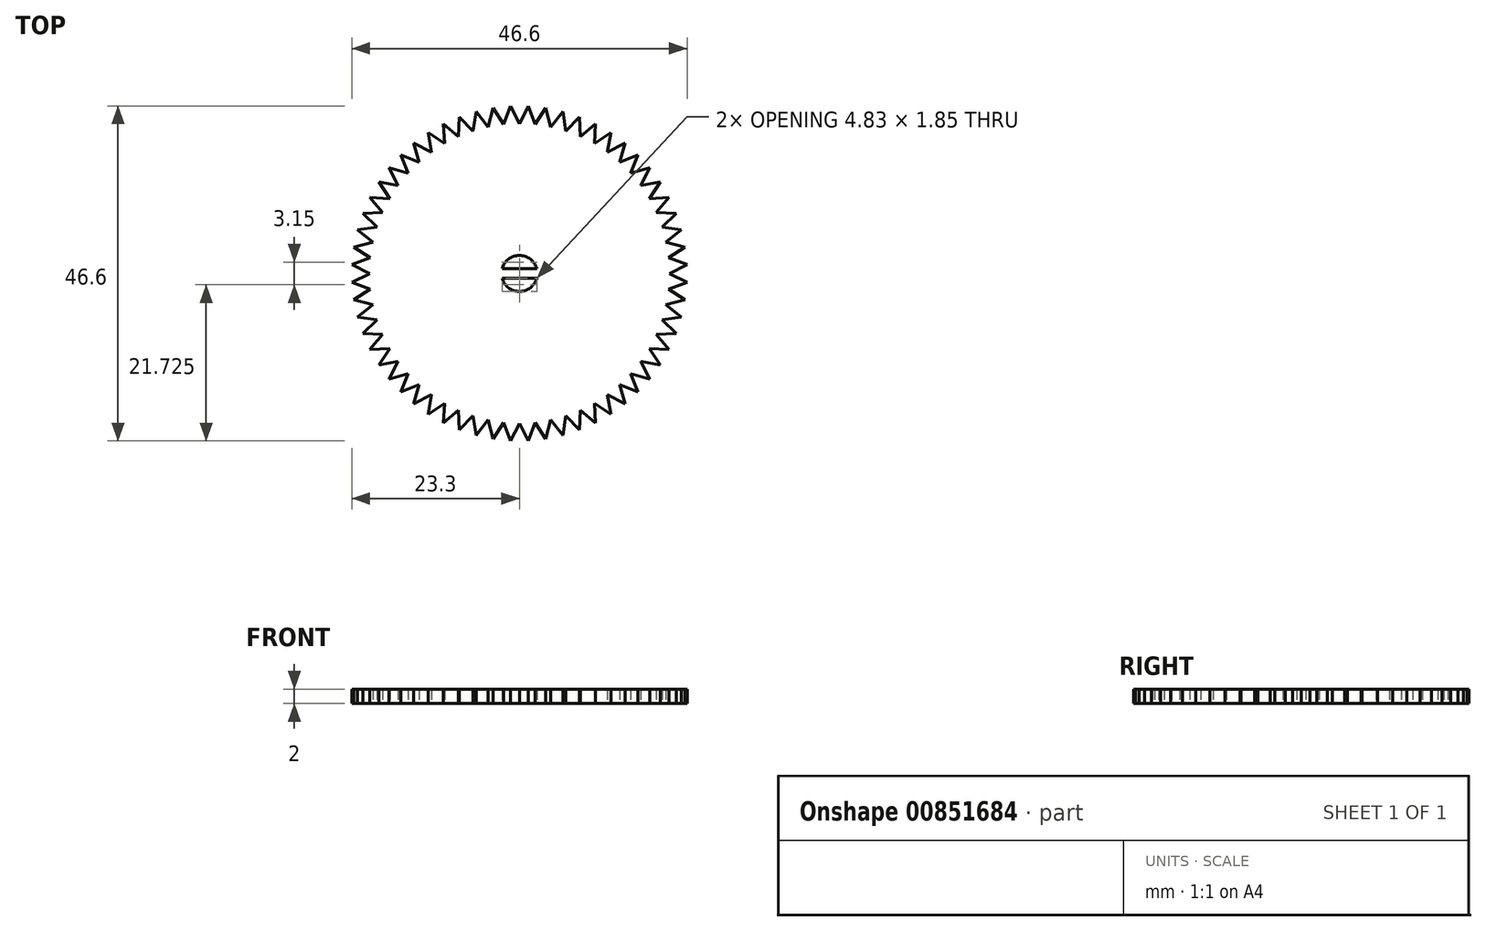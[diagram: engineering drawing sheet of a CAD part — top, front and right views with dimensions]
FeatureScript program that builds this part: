
annotation { "Feature Type Name" : "Feature", "Feature Type Description" : "" }
export const myFeature = defineFeature(function(context is Context, id is Id, definition is map)
    precondition{}
    {
        {
            var Q0;
            Q0=qCreatedBy(makeId("Top.planeOp"),FACE);
            var sketch = newSketch(context, id + "F0", { "sketchPlane" : qUnion([Q0])});
            skLineSegment(sketch, "E0", {"start": v(0, 0) * mm, "end": v(0, 24.66) * mm, "construction": true});
            skLineSegment(sketch, "E1", {"start": v(0, 0) * mm, "end": v(1.3, 24.64) * mm, "construction": true});
            skLineSegment(sketch, "E2", {"start": v(0, 0) * mm, "end": v(2.57, 24.5) * mm, "construction": true});
            skLineSegment(sketch, "E3", {"start": v(0, 20.83) * mm, "end": v(1.22, 23.3) * mm});
            skLineSegment(sketch, "E4", {"start": v(1.22, 23.3) * mm, "end": v(2.18, 20.71) * mm});
            skLineSegment(sketch, "E5.1.0", {"start": v(-2.18, 20.71) * mm, "end": v(-1.22, 23.3) * mm});
            skLineSegment(sketch, "E5.1.1", {"start": v(-1.22, 23.3) * mm, "end": v(0, 20.83) * mm});
            skLineSegment(sketch, "E5.2.0", {"start": v(-4.33, 20.37) * mm, "end": v(-3.65, 23.04) * mm});
            skLineSegment(sketch, "E5.2.1", {"start": v(-3.65, 23.04) * mm, "end": v(-2.18, 20.71) * mm});
            skLineSegment(sketch, "E5.3.0", {"start": v(-6.44, 19.8) * mm, "end": v(-6.04, 22.53) * mm});
            skLineSegment(sketch, "E5.3.1", {"start": v(-6.04, 22.53) * mm, "end": v(-4.33, 20.37) * mm});
            skLineSegment(sketch, "E5.4.0", {"start": v(-8.47, 19.03) * mm, "end": v(-8.36, 21.78) * mm});
            skLineSegment(sketch, "E5.4.1", {"start": v(-8.36, 21.78) * mm, "end": v(-6.44, 19.8) * mm});
            skLineSegment(sketch, "E5.5.0", {"start": v(-10.41, 18.04) * mm, "end": v(-10.6, 20.78) * mm});
            skLineSegment(sketch, "E5.5.1", {"start": v(-10.6, 20.78) * mm, "end": v(-8.47, 19.03) * mm});
            skLineSegment(sketch, "E5.6.0", {"start": v(-12.24, 16.85) * mm, "end": v(-12.7, 19.56) * mm});
            skLineSegment(sketch, "E5.6.1", {"start": v(-12.7, 19.56) * mm, "end": v(-10.41, 18.04) * mm});
            skLineSegment(sketch, "E5.7.0", {"start": v(-13.94, 15.48) * mm, "end": v(-14.68, 18.13) * mm});
            skLineSegment(sketch, "E5.7.1", {"start": v(-14.68, 18.13) * mm, "end": v(-12.24, 16.85) * mm});
            skLineSegment(sketch, "E5.8.0", {"start": v(-15.48, 13.94) * mm, "end": v(-16.5, 16.5) * mm});
            skLineSegment(sketch, "E5.8.1", {"start": v(-16.5, 16.5) * mm, "end": v(-13.94, 15.48) * mm});
            skLineSegment(sketch, "E5.9.0", {"start": v(-16.85, 12.24) * mm, "end": v(-18.13, 14.68) * mm});
            skLineSegment(sketch, "E5.9.1", {"start": v(-18.13, 14.68) * mm, "end": v(-15.48, 13.94) * mm});
            skLineSegment(sketch, "E5.10.0", {"start": v(-18.04, 10.41) * mm, "end": v(-19.56, 12.7) * mm});
            skLineSegment(sketch, "E5.10.1", {"start": v(-19.56, 12.7) * mm, "end": v(-16.85, 12.24) * mm});
            skLineSegment(sketch, "E5.11.0", {"start": v(-19.03, 8.47) * mm, "end": v(-20.78, 10.6) * mm});
            skLineSegment(sketch, "E5.11.1", {"start": v(-20.78, 10.6) * mm, "end": v(-18.04, 10.41) * mm});
            skLineSegment(sketch, "E5.12.0", {"start": v(-19.8, 6.44) * mm, "end": v(-21.78, 8.36) * mm});
            skLineSegment(sketch, "E5.12.1", {"start": v(-21.78, 8.36) * mm, "end": v(-19.03, 8.47) * mm});
            skLineSegment(sketch, "E5.13.0", {"start": v(-20.37, 4.33) * mm, "end": v(-22.53, 6.04) * mm});
            skLineSegment(sketch, "E5.13.1", {"start": v(-22.53, 6.04) * mm, "end": v(-19.8, 6.44) * mm});
            skLineSegment(sketch, "E5.14.0", {"start": v(-20.71, 2.18) * mm, "end": v(-23.04, 3.65) * mm});
            skLineSegment(sketch, "E5.14.1", {"start": v(-23.04, 3.65) * mm, "end": v(-20.37, 4.33) * mm});
            skLineSegment(sketch, "E5.15.0", {"start": v(-20.83, 0) * mm, "end": v(-23.3, 1.22) * mm});
            skLineSegment(sketch, "E5.15.1", {"start": v(-23.3, 1.22) * mm, "end": v(-20.71, 2.18) * mm});
            skLineSegment(sketch, "E5.16.0", {"start": v(-20.71, -2.18) * mm, "end": v(-23.3, -1.22) * mm});
            skLineSegment(sketch, "E5.16.1", {"start": v(-23.3, -1.22) * mm, "end": v(-20.83, 0) * mm});
            skLineSegment(sketch, "E5.17.0", {"start": v(-20.37, -4.33) * mm, "end": v(-23.04, -3.65) * mm});
            skLineSegment(sketch, "E5.17.1", {"start": v(-23.04, -3.65) * mm, "end": v(-20.71, -2.18) * mm});
            skLineSegment(sketch, "E5.18.0", {"start": v(-19.8, -6.44) * mm, "end": v(-22.53, -6.04) * mm});
            skLineSegment(sketch, "E5.18.1", {"start": v(-22.53, -6.04) * mm, "end": v(-20.37, -4.33) * mm});
            skLineSegment(sketch, "E5.19.0", {"start": v(-19.03, -8.47) * mm, "end": v(-21.78, -8.36) * mm});
            skLineSegment(sketch, "E5.19.1", {"start": v(-21.78, -8.36) * mm, "end": v(-19.8, -6.44) * mm});
            skLineSegment(sketch, "E5.20.0", {"start": v(-18.04, -10.41) * mm, "end": v(-20.78, -10.6) * mm});
            skLineSegment(sketch, "E5.20.1", {"start": v(-20.78, -10.6) * mm, "end": v(-19.03, -8.47) * mm});
            skLineSegment(sketch, "E5.21.0", {"start": v(-16.85, -12.24) * mm, "end": v(-19.56, -12.7) * mm});
            skLineSegment(sketch, "E5.21.1", {"start": v(-19.56, -12.7) * mm, "end": v(-18.04, -10.41) * mm});
            skLineSegment(sketch, "E5.22.0", {"start": v(-15.48, -13.94) * mm, "end": v(-18.13, -14.68) * mm});
            skLineSegment(sketch, "E5.22.1", {"start": v(-18.13, -14.68) * mm, "end": v(-16.85, -12.24) * mm});
            skLineSegment(sketch, "E5.23.0", {"start": v(-13.94, -15.48) * mm, "end": v(-16.5, -16.5) * mm});
            skLineSegment(sketch, "E5.23.1", {"start": v(-16.5, -16.5) * mm, "end": v(-15.48, -13.94) * mm});
            skLineSegment(sketch, "E5.24.0", {"start": v(-12.24, -16.85) * mm, "end": v(-14.68, -18.13) * mm});
            skLineSegment(sketch, "E5.24.1", {"start": v(-14.68, -18.13) * mm, "end": v(-13.94, -15.48) * mm});
            skLineSegment(sketch, "E5.25.0", {"start": v(-10.41, -18.04) * mm, "end": v(-12.7, -19.56) * mm});
            skLineSegment(sketch, "E5.25.1", {"start": v(-12.7, -19.56) * mm, "end": v(-12.24, -16.85) * mm});
            skLineSegment(sketch, "E5.26.0", {"start": v(-8.47, -19.03) * mm, "end": v(-10.6, -20.78) * mm});
            skLineSegment(sketch, "E5.26.1", {"start": v(-10.6, -20.78) * mm, "end": v(-10.41, -18.04) * mm});
            skLineSegment(sketch, "E5.27.0", {"start": v(-6.44, -19.8) * mm, "end": v(-8.36, -21.78) * mm});
            skLineSegment(sketch, "E5.27.1", {"start": v(-8.36, -21.78) * mm, "end": v(-8.47, -19.03) * mm});
            skLineSegment(sketch, "E5.28.0", {"start": v(-4.33, -20.37) * mm, "end": v(-6.04, -22.53) * mm});
            skLineSegment(sketch, "E5.28.1", {"start": v(-6.04, -22.53) * mm, "end": v(-6.44, -19.8) * mm});
            skLineSegment(sketch, "E5.29.0", {"start": v(-2.18, -20.71) * mm, "end": v(-3.65, -23.04) * mm});
            skLineSegment(sketch, "E5.29.1", {"start": v(-3.65, -23.04) * mm, "end": v(-4.33, -20.37) * mm});
            skLineSegment(sketch, "E5.30.0", {"start": v(0, -20.83) * mm, "end": v(-1.22, -23.3) * mm});
            skLineSegment(sketch, "E5.30.1", {"start": v(-1.22, -23.3) * mm, "end": v(-2.18, -20.71) * mm});
            skLineSegment(sketch, "E5.31.0", {"start": v(2.18, -20.71) * mm, "end": v(1.22, -23.3) * mm});
            skLineSegment(sketch, "E5.31.1", {"start": v(1.22, -23.3) * mm, "end": v(0, -20.83) * mm});
            skLineSegment(sketch, "E5.32.0", {"start": v(4.33, -20.37) * mm, "end": v(3.65, -23.04) * mm});
            skLineSegment(sketch, "E5.32.1", {"start": v(3.65, -23.04) * mm, "end": v(2.18, -20.71) * mm});
            skLineSegment(sketch, "E5.33.0", {"start": v(6.44, -19.8) * mm, "end": v(6.04, -22.53) * mm});
            skLineSegment(sketch, "E5.33.1", {"start": v(6.04, -22.53) * mm, "end": v(4.33, -20.37) * mm});
            skLineSegment(sketch, "E5.34.0", {"start": v(8.47, -19.03) * mm, "end": v(8.36, -21.78) * mm});
            skLineSegment(sketch, "E5.34.1", {"start": v(8.36, -21.78) * mm, "end": v(6.44, -19.8) * mm});
            skLineSegment(sketch, "E5.35.0", {"start": v(10.41, -18.04) * mm, "end": v(10.6, -20.78) * mm});
            skLineSegment(sketch, "E5.35.1", {"start": v(10.6, -20.78) * mm, "end": v(8.47, -19.03) * mm});
            skLineSegment(sketch, "E5.36.0", {"start": v(12.24, -16.85) * mm, "end": v(12.7, -19.56) * mm});
            skLineSegment(sketch, "E5.36.1", {"start": v(12.7, -19.56) * mm, "end": v(10.41, -18.04) * mm});
            skLineSegment(sketch, "E5.37.0", {"start": v(13.94, -15.48) * mm, "end": v(14.68, -18.13) * mm});
            skLineSegment(sketch, "E5.37.1", {"start": v(14.68, -18.13) * mm, "end": v(12.24, -16.85) * mm});
            skLineSegment(sketch, "E5.38.0", {"start": v(15.48, -13.94) * mm, "end": v(16.5, -16.5) * mm});
            skLineSegment(sketch, "E5.38.1", {"start": v(16.5, -16.5) * mm, "end": v(13.94, -15.48) * mm});
            skLineSegment(sketch, "E5.39.0", {"start": v(16.85, -12.24) * mm, "end": v(18.13, -14.68) * mm});
            skLineSegment(sketch, "E5.39.1", {"start": v(18.13, -14.68) * mm, "end": v(15.48, -13.94) * mm});
            skLineSegment(sketch, "E5.40.0", {"start": v(18.04, -10.41) * mm, "end": v(19.56, -12.7) * mm});
            skLineSegment(sketch, "E5.40.1", {"start": v(19.56, -12.7) * mm, "end": v(16.85, -12.24) * mm});
            skLineSegment(sketch, "E5.41.0", {"start": v(19.03, -8.47) * mm, "end": v(20.78, -10.6) * mm});
            skLineSegment(sketch, "E5.41.1", {"start": v(20.78, -10.6) * mm, "end": v(18.04, -10.41) * mm});
            skLineSegment(sketch, "E5.42.0", {"start": v(19.8, -6.44) * mm, "end": v(21.78, -8.36) * mm});
            skLineSegment(sketch, "E5.42.1", {"start": v(21.78, -8.36) * mm, "end": v(19.03, -8.47) * mm});
            skLineSegment(sketch, "E5.43.0", {"start": v(20.37, -4.33) * mm, "end": v(22.53, -6.04) * mm});
            skLineSegment(sketch, "E5.43.1", {"start": v(22.53, -6.04) * mm, "end": v(19.8, -6.44) * mm});
            skLineSegment(sketch, "E5.44.0", {"start": v(20.71, -2.18) * mm, "end": v(23.04, -3.65) * mm});
            skLineSegment(sketch, "E5.44.1", {"start": v(23.04, -3.65) * mm, "end": v(20.37, -4.33) * mm});
            skLineSegment(sketch, "E5.45.0", {"start": v(20.83, 0) * mm, "end": v(23.3, -1.22) * mm});
            skLineSegment(sketch, "E5.45.1", {"start": v(23.3, -1.22) * mm, "end": v(20.71, -2.18) * mm});
            skLineSegment(sketch, "E5.46.0", {"start": v(20.71, 2.18) * mm, "end": v(23.3, 1.22) * mm});
            skLineSegment(sketch, "E5.46.1", {"start": v(23.3, 1.22) * mm, "end": v(20.83, 0) * mm});
            skLineSegment(sketch, "E5.47.0", {"start": v(20.37, 4.33) * mm, "end": v(23.04, 3.65) * mm});
            skLineSegment(sketch, "E5.47.1", {"start": v(23.04, 3.65) * mm, "end": v(20.71, 2.18) * mm});
            skLineSegment(sketch, "E5.48.0", {"start": v(19.8, 6.44) * mm, "end": v(22.53, 6.04) * mm});
            skLineSegment(sketch, "E5.48.1", {"start": v(22.53, 6.04) * mm, "end": v(20.37, 4.33) * mm});
            skLineSegment(sketch, "E5.49.0", {"start": v(19.03, 8.47) * mm, "end": v(21.78, 8.36) * mm});
            skLineSegment(sketch, "E5.49.1", {"start": v(21.78, 8.36) * mm, "end": v(19.8, 6.44) * mm});
            skLineSegment(sketch, "E5.50.0", {"start": v(18.04, 10.41) * mm, "end": v(20.78, 10.6) * mm});
            skLineSegment(sketch, "E5.50.1", {"start": v(20.78, 10.6) * mm, "end": v(19.03, 8.47) * mm});
            skLineSegment(sketch, "E5.51.0", {"start": v(16.85, 12.24) * mm, "end": v(19.56, 12.7) * mm});
            skLineSegment(sketch, "E5.51.1", {"start": v(19.56, 12.7) * mm, "end": v(18.04, 10.41) * mm});
            skLineSegment(sketch, "E5.52.0", {"start": v(15.48, 13.94) * mm, "end": v(18.13, 14.68) * mm});
            skLineSegment(sketch, "E5.52.1", {"start": v(18.13, 14.68) * mm, "end": v(16.85, 12.24) * mm});
            skLineSegment(sketch, "E5.53.0", {"start": v(13.94, 15.48) * mm, "end": v(16.5, 16.5) * mm});
            skLineSegment(sketch, "E5.53.1", {"start": v(16.5, 16.5) * mm, "end": v(15.48, 13.94) * mm});
            skLineSegment(sketch, "E5.54.0", {"start": v(12.24, 16.85) * mm, "end": v(14.68, 18.13) * mm});
            skLineSegment(sketch, "E5.54.1", {"start": v(14.68, 18.13) * mm, "end": v(13.94, 15.48) * mm});
            skLineSegment(sketch, "E5.55.0", {"start": v(10.41, 18.04) * mm, "end": v(12.7, 19.56) * mm});
            skLineSegment(sketch, "E5.55.1", {"start": v(12.7, 19.56) * mm, "end": v(12.24, 16.85) * mm});
            skLineSegment(sketch, "E5.56.0", {"start": v(8.47, 19.03) * mm, "end": v(10.6, 20.78) * mm});
            skLineSegment(sketch, "E5.56.1", {"start": v(10.6, 20.78) * mm, "end": v(10.41, 18.04) * mm});
            skLineSegment(sketch, "E5.57.0", {"start": v(6.44, 19.8) * mm, "end": v(8.36, 21.78) * mm});
            skLineSegment(sketch, "E5.57.1", {"start": v(8.36, 21.78) * mm, "end": v(8.47, 19.03) * mm});
            skLineSegment(sketch, "E5.58.0", {"start": v(4.33, 20.37) * mm, "end": v(6.04, 22.53) * mm});
            skLineSegment(sketch, "E5.58.1", {"start": v(6.04, 22.53) * mm, "end": v(6.44, 19.8) * mm});
            skLineSegment(sketch, "E5.59.0", {"start": v(2.18, 20.71) * mm, "end": v(3.65, 23.04) * mm});
            skLineSegment(sketch, "E5.59.1", {"start": v(3.65, 23.04) * mm, "end": v(4.33, 20.37) * mm});
            skPoint(sketch, "E5.center", {"position": v(0, 0) * mm});
            skArc(sketch, "E6", {"start": v(2.41, 0.65) * mm, "mid": v(0, 2.5) * mm, "end": v(-2.41, 0.65) * mm});
            skLineSegment(sketch, "E7.bottom", {"start": v(2.41, -0.65) * mm, "end": v(-2.41, -0.65) * mm});
            skLineSegment(sketch, "E7.top", {"start": v(2.41, 0.65) * mm, "end": v(-2.41, 0.65) * mm});
            skPoint(sketch, "E7.right.end.orphan", {"position": v(-4.05, 0.65) * mm});
            skPoint(sketch, "E7.right.start.orphan", {"position": v(-4.05, -0.65) * mm});
            skPoint(sketch, "E8.orphan", {"position": v(4.05, 0.65) * mm});
            skPoint(sketch, "E9.orphan", {"position": v(4.05, -0.65) * mm});
            skArc(sketch, "E10.trimOffspring", {"start": v(-2.41, -0.65) * mm, "mid": v(0, -2.5) * mm, "end": v(2.41, -0.65) * mm});
            skSolve(sketch);
        }
        {
            var Q0;
            Q0=makeQuery(id+"F0.imprint","IMPRINT",FACE,{"disambiguationData":[TD([[makeQuery(id+"F0.imprint","IMPRINT",EDGE,{"derivedFrom":sQuery(id+"F0.wireOp",EDGE,"E3")}),-1.0]])]});
            extrude(context, id + "F1", {"entities" : qUnion([Q0]), "depth" : 2 * mm, "offsetDistance" : 25 * mm});
        }
    });
